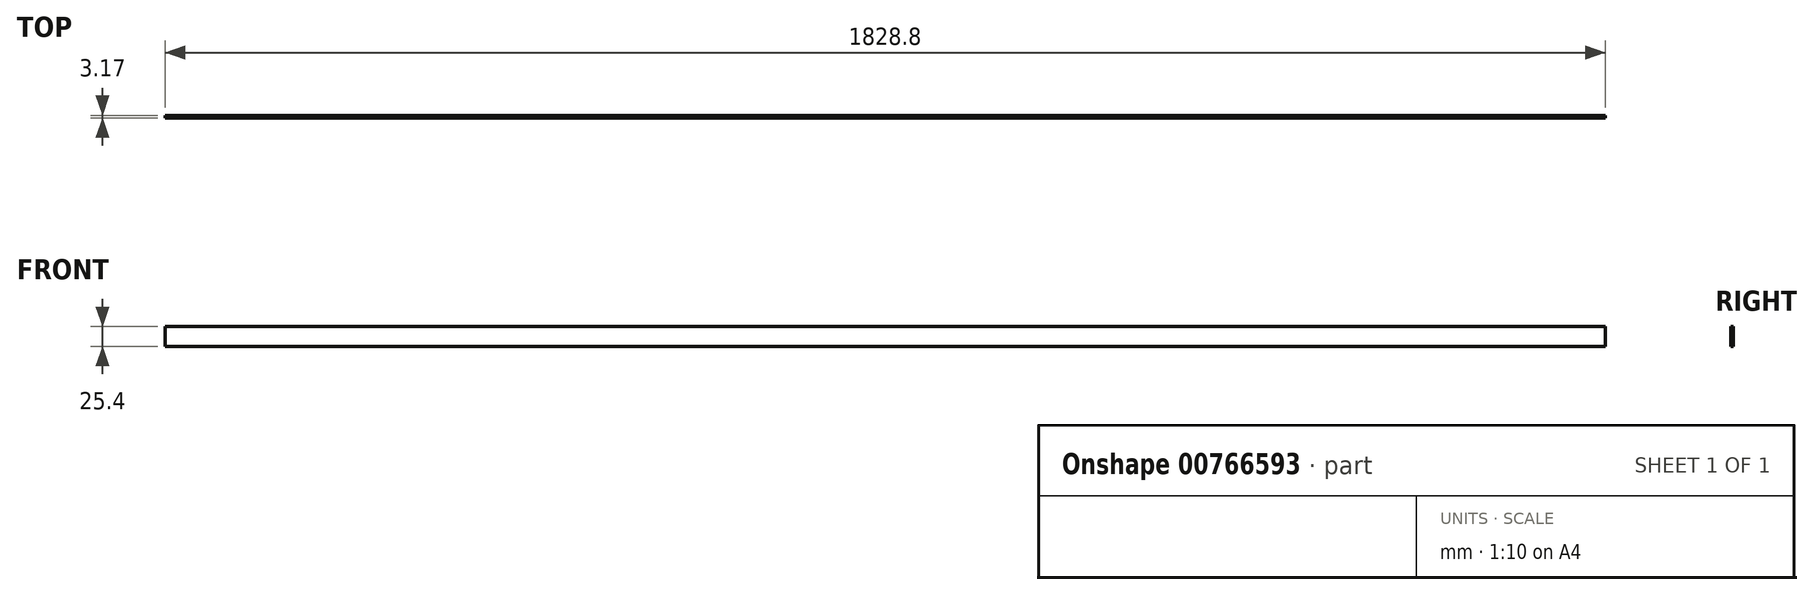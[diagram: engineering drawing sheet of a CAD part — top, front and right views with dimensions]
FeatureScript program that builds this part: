
annotation { "Feature Type Name" : "Feature", "Feature Type Description" : "" }
export const myFeature = defineFeature(function(context is Context, id is Id, definition is map)
    precondition{}
    {
        {
            var Q0;
            Q0=qCreatedBy(makeId("Front.planeOp"),FACE);
            var sketch = newSketch(context, id + "F0", { "sketchPlane" : qUnion([Q0])});
            skLineSegment(sketch, "E0.bottom", {"start": v(0, 0) * mm, "end": v(-1828.8, 0) * mm});
            skLineSegment(sketch, "E0.top", {"start": v(0, 25.4) * mm, "end": v(-1828.8, 25.4) * mm});
            skLineSegment(sketch, "E0.left", {"start": v(0, 0) * mm, "end": v(0, 25.4) * mm});
            skLineSegment(sketch, "E0.right", {"start": v(-1828.8, 0) * mm, "end": v(-1828.8, 25.4) * mm});
            skSolve(sketch);
        }
        {
            var Q0;
            Q0 = qSketchRegion(id + "F0", true);
            extrude(context, id + "F1", {"entities" : qUnion([Q0]), "depth" : 3.17 * mm, "offsetDistance" : 25.4 * mm});
        }
        {
            var Q0;
            Q0=makeQuery(id+"F1.opExtrude","CAP_FACE",FACE,{"disambiguationData":[OSD([sQuery(id+"F0.wireOp",EDGE,"E0.bottom"),sQuery(id+"F0.wireOp",EDGE,"E0.top"),sQuery(id+"F0.wireOp",EDGE,"E0.left"),sQuery(id+"F0.wireOp",EDGE,"E0.right")])],"isStart":true});
            var sketch = newSketch(context, id + "F2", { "sketchPlane" : qUnion([Q0])});
            skCircle(sketch, "E1", {"center": v(50.8, 12.7) * mm, "radius": 4.76 * mm});
            skSolve(sketch);
        }
        {
            var Q0;
            Q0=makeQuery(id+"F2.imprint","IMPRINT",FACE,{"disambiguationData":[TD([[makeQuery(id+"F2.imprint","IMPRINT",EDGE,{"derivedFrom":sQuery(id+"F2.wireOp",EDGE,"E1")}),-1.0]])]});
            var sketch = newSketch(context, id + "F3", { "sketchPlane" : qUnion([Q0])});
            skCircle(sketch, "E2", {"center": v(1778, 12.7) * mm, "radius": 4.76 * mm});
            skSolve(sketch);
        }
    });
